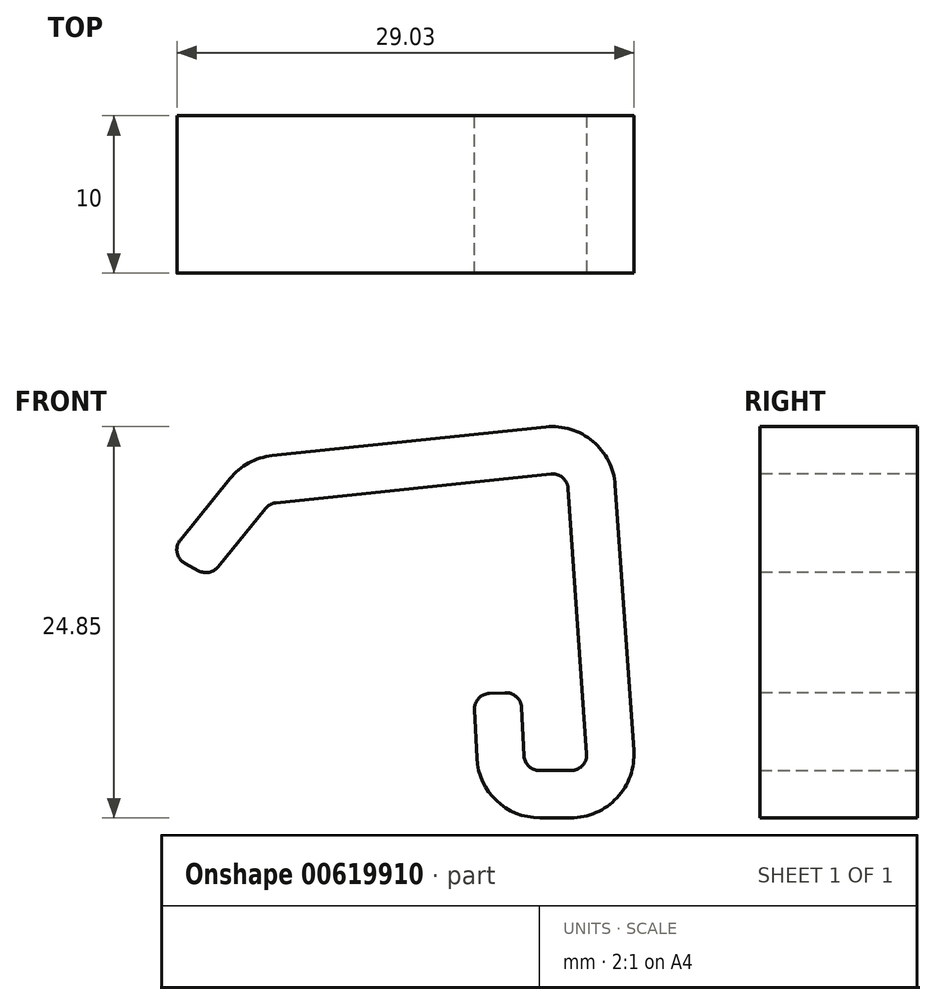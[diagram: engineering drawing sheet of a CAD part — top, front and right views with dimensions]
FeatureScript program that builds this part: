
annotation { "Feature Type Name" : "Feature", "Feature Type Description" : "" }
export const myFeature = defineFeature(function(context is Context, id is Id, definition is map)
    precondition{}
    {
        {
            var Q0;
            Q0=qCreatedBy(makeId("Front.planeOp"),FACE);
            var sketch = newSketch(context, id + "F0", { "sketchPlane" : qUnion([Q0])});
            skLineSegment(sketch, "E0", {"start": v(30.66, 13.32) * mm, "end": v(30.92, 8.32) * mm});
            skLineSegment(sketch, "E1", {"start": v(30.92, 8.32) * mm, "end": v(34.92, 8.32) * mm});
            skLineSegment(sketch, "E2", {"start": v(34.92, 8.32) * mm, "end": v(33.6, 27.27) * mm});
            skLineSegment(sketch, "E3", {"start": v(36.37, 30.58) * mm, "end": v(38.14, 5.32) * mm});
            skLineSegment(sketch, "E4", {"start": v(30.66, 13.32) * mm, "end": v(27.66, 13.16) * mm});
            skLineSegment(sketch, "E5", {"start": v(27.66, 13.16) * mm, "end": v(28.07, 5.32) * mm});
            skLineSegment(sketch, "E6", {"start": v(28.07, 5.32) * mm, "end": v(38.14, 5.32) * mm});
            skLineSegment(sketch, "E7", {"start": v(33.6, 27.27) * mm, "end": v(14.7, 25.29) * mm});
            skLineSegment(sketch, "E8", {"start": v(14.7, 25.29) * mm, "end": v(10.92, 20.63) * mm});
            skLineSegment(sketch, "E9", {"start": v(36.37, 30.58) * mm, "end": v(13.23, 28.15) * mm});
            skLineSegment(sketch, "E10", {"start": v(13.23, 28.15) * mm, "end": v(8.28, 22.04) * mm});
            skLineSegment(sketch, "E11", {"start": v(8.28, 22.04) * mm, "end": v(10.92, 20.63) * mm});
            skSolve(sketch);
        }
        {
            var Q0;
            Q0=makeQuery(id+"F0.imprint","IMPRINT",FACE,{"disambiguationData":[TD([[makeQuery(id+"F0.imprint","IMPRINT",EDGE,{"derivedFrom":sQuery(id+"F0.wireOp",EDGE,"E0")}),-1.0]])]});
            extrude(context, id + "F1", {"entities" : qUnion([Q0]), "depth" : 10 * mm, "offsetDistance" : 25 * mm});
        }
        {
            var Q0;
            Q0=makeQuery(id+"F1.opExtrude","SWEPT_EDGE",EDGE,{"disambiguationData":[OSD([sQuery(id+"F0.wireOp",EDGE,"z5vzFcr0-TTuV-Ur5p-8CuR-3FNruGozkA39"),sQuery(id+"F0.wireOp",EDGE,"tScNbiU7-jUDc-luHU-Ofxr-aMvohJIte3Ij")])]});
            var Q1;
            Q1=makeQuery(id+"F1.opExtrude","SWEPT_EDGE",EDGE,{"disambiguationData":[OSD([sQuery(id+"F0.wireOp",EDGE,"E2"),sQuery(id+"F0.wireOp",EDGE,"z5vzFcr0-TTuV-Ur5p-8CuR-3FNruGozkA39")])]});
            var Q2;
            Q2=makeQuery(id+"F1.opExtrude","SWEPT_EDGE",EDGE,{"disambiguationData":[OSD([sQuery(id+"F0.wireOp",EDGE,"E1"),sQuery(id+"F0.wireOp",EDGE,"E2")])]});
            var Q3;
            Q3=makeQuery(id+"F1.opExtrude","SWEPT_EDGE",EDGE,{"disambiguationData":[OSD([sQuery(id+"F0.wireOp",EDGE,"E0"),sQuery(id+"F0.wireOp",EDGE,"E1")])]});
            var Q4;
            Q4=makeQuery(id+"F1.opExtrude","SWEPT_EDGE",EDGE,{"disambiguationData":[OSD([sQuery(id+"F0.wireOp",EDGE,"E7"),sQuery(id+"F0.wireOp",EDGE,"E8")])]});
            fillet(context, id + "F2", {"entities" : qUnion([Q0, Q1, Q2, Q3, Q4]), "radius" : 1 * mm, "tangentPropagation" : true, "allowEdgeOverflow" : false});
        }
        {
            var Q0;
            Q0=makeQuery(id+"F1.opExtrude","SWEPT_EDGE",EDGE,{"disambiguationData":[OSD([sQuery(id+"F0.wireOp",EDGE,"rZcDTGZm-K0Wo-fHCp-oR4G-TDA54O32Uf16"),sQuery(id+"F0.wireOp",EDGE,"8m45i2SR-QPBe-mXot-X4Nl-QCXT3eAMN7fl")])]});
            var Q1;
            Q1=makeQuery(id+"F1.opExtrude","SWEPT_EDGE",EDGE,{"disambiguationData":[OSD([sQuery(id+"F0.wireOp",EDGE,"E3"),sQuery(id+"F0.wireOp",EDGE,"8m45i2SR-QPBe-mXot-X4Nl-QCXT3eAMN7fl")])]});
            var Q2;
            Q2=makeQuery(id+"F1.opExtrude","SWEPT_EDGE",EDGE,{"disambiguationData":[OSD([sQuery(id+"F0.wireOp",EDGE,"E3"),sQuery(id+"F0.wireOp",EDGE,"E6")])]});
            var Q3;
            Q3=makeQuery(id+"F1.opExtrude","SWEPT_EDGE",EDGE,{"disambiguationData":[OSD([sQuery(id+"F0.wireOp",EDGE,"E5"),sQuery(id+"F0.wireOp",EDGE,"E6")])]});
            var Q4;
            Q4=makeQuery(id+"F1.opExtrude","SWEPT_EDGE",EDGE,{"disambiguationData":[OSD([sQuery(id+"F0.wireOp",EDGE,"E9"),sQuery(id+"F0.wireOp",EDGE,"E10")])]});
            fillet(context, id + "F3", {"entities" : qUnion([Q0, Q1, Q2, Q3, Q4]), "radius" : 4 * mm, "tangentPropagation" : true, "allowEdgeOverflow" : false});
        }
        {
            var Q0;
            Q0=makeQuery(id+"F1.opExtrude","SWEPT_EDGE",EDGE,{"disambiguationData":[OSD([sQuery(id+"F0.wireOp",EDGE,"rZcDTGZm-K0Wo-fHCp-oR4G-TDA54O32Uf16"),sQuery(id+"F0.wireOp",EDGE,"PeCG5VBA-lL8u-FB2p-3mDr-MbDpzb7DcBio")])]});
            var Q1;
            Q1=makeQuery(id+"F1.opExtrude","SWEPT_EDGE",EDGE,{"disambiguationData":[OSD([sQuery(id+"F0.wireOp",EDGE,"tScNbiU7-jUDc-luHU-Ofxr-aMvohJIte3Ij"),sQuery(id+"F0.wireOp",EDGE,"PeCG5VBA-lL8u-FB2p-3mDr-MbDpzb7DcBio")])]});
            var Q2;
            Q2=makeQuery(id+"F1.opExtrude","SWEPT_EDGE",EDGE,{"disambiguationData":[OSD([sQuery(id+"F0.wireOp",EDGE,"E4"),sQuery(id+"F0.wireOp",EDGE,"E5")])]});
            var Q3;
            Q3=makeQuery(id+"F1.opExtrude","SWEPT_EDGE",EDGE,{"disambiguationData":[OSD([sQuery(id+"F0.wireOp",EDGE,"E0"),sQuery(id+"F0.wireOp",EDGE,"E4")])]});
            var Q4;
            Q4=makeQuery(id+"F1.opExtrude","SWEPT_EDGE",EDGE,{"disambiguationData":[OSD([sQuery(id+"F0.wireOp",EDGE,"E10"),sQuery(id+"F0.wireOp",EDGE,"E11")])]});
            var Q5;
            Q5=makeQuery(id+"F1.opExtrude","SWEPT_EDGE",EDGE,{"disambiguationData":[OSD([sQuery(id+"F0.wireOp",EDGE,"E8"),sQuery(id+"F0.wireOp",EDGE,"E11")])]});
            fillet(context, id + "F4", {"entities" : qUnion([Q0, Q1, Q2, Q3, Q4, Q5]), "radius" : 1 * mm, "tangentPropagation" : true, "allowEdgeOverflow" : false});
        }
    });
